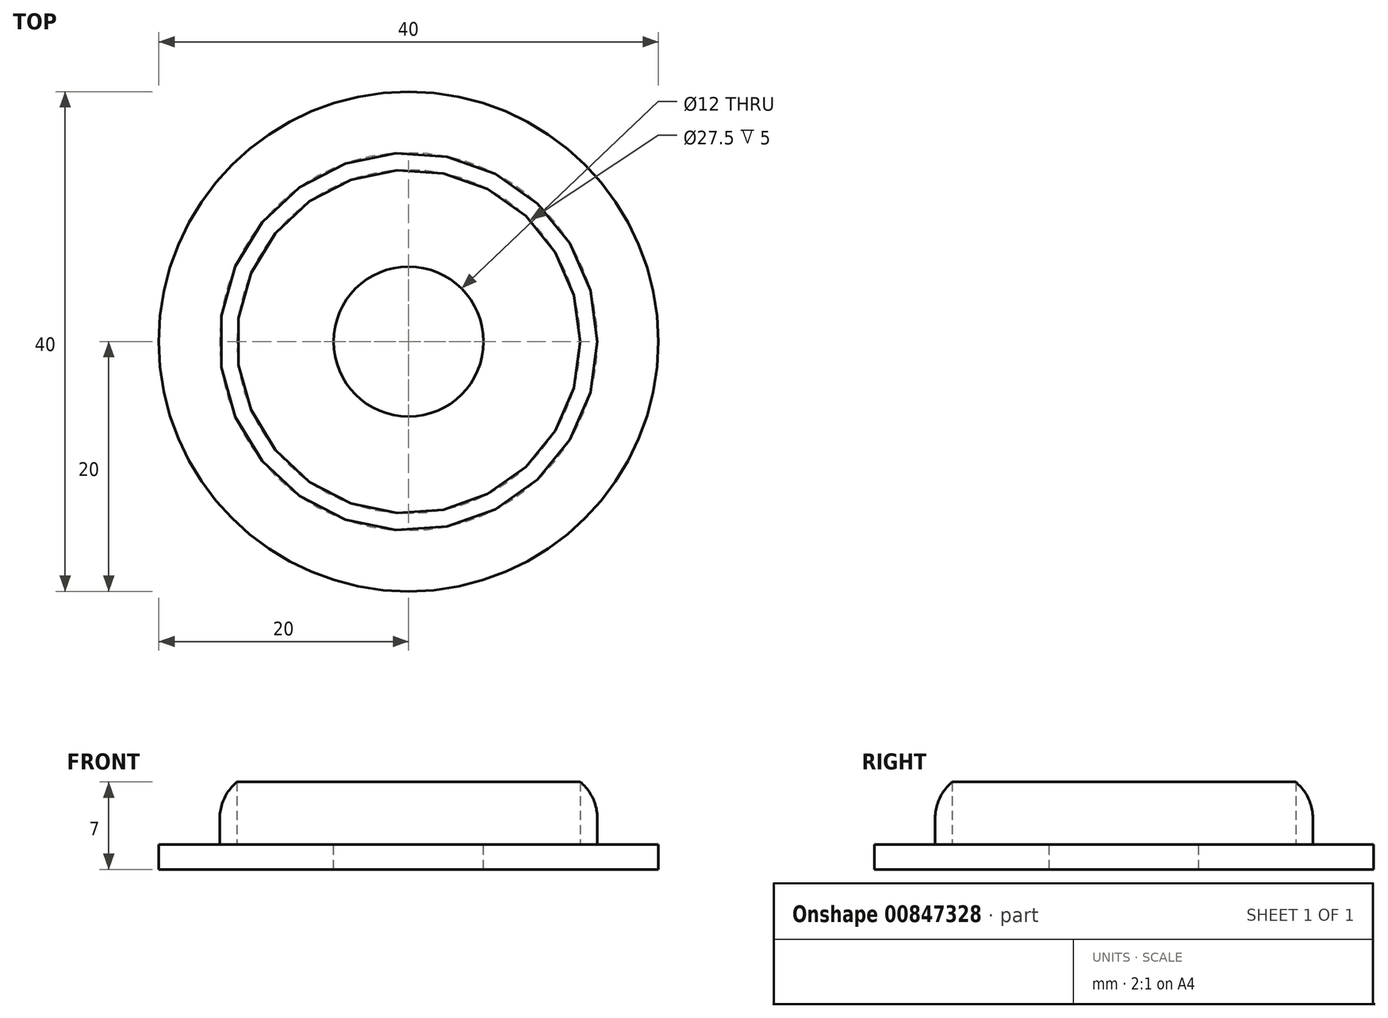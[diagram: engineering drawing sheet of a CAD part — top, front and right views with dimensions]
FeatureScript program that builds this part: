
annotation { "Feature Type Name" : "Feature", "Feature Type Description" : "" }
export const myFeature = defineFeature(function(context is Context, id is Id, definition is map)
    precondition{}
    {
        {
            var Q0;
            Q0=qCreatedBy(makeId("Top.planeOp"),FACE);
            var sketch = newSketch(context, id + "F0", { "sketchPlane" : qUnion([Q0])});
            skCircle(sketch, "E0", {"center": v(0, 0) * mm, "radius": 15.12 * mm});
            skCircle(sketch, "E1", {"center": v(0, 0) * mm, "radius": 20 * mm});
            skCircle(sketch, "E2", {"center": v(0, 0) * mm, "radius": 13.75 * mm});
            skCircle(sketch, "E3", {"center": v(0, 0) * mm, "radius": 6 * mm});
            skSolve(sketch);
        }
        {
            var Q0;
            Q0=makeQuery(id+"F0.imprint","IMPRINT",FACE,{"disambiguationData":[TD([[makeQuery(id+"F0.imprint","IMPRINT",EDGE,{"derivedFrom":sQuery(id+"F0.wireOp",EDGE,"E0")}),1.0]])]});
            extrude(context, id + "F1", {"entities" : qUnion([Q0]), "depth" : 5 * mm, "offsetDistance" : 25 * mm});
        }
        {
            var Q0;
            Q0=makeQuery(id+"F0.imprint","IMPRINT",FACE,{"disambiguationData":[TD([[makeQuery(id+"F0.imprint","IMPRINT",EDGE,{"derivedFrom":sQuery(id+"F0.wireOp",EDGE,"E0")}),1.0]])]});
            var Q1;
            Q1=makeQuery(id+"F0.imprint","IMPRINT",FACE,{"disambiguationData":[TD([[makeQuery(id+"F0.imprint","IMPRINT",EDGE,{"derivedFrom":sQuery(id+"F0.wireOp",EDGE,"E0")}),-1.0]])]});
            var Q2;
            Q2=makeQuery(id+"F0.imprint","IMPRINT",FACE,{"disambiguationData":[TD([[makeQuery(id+"F0.imprint","IMPRINT",EDGE,{"derivedFrom":sQuery(id+"F0.wireOp",EDGE,"E2")}),1.0]])]});
            extrude(context, id + "F2", {"entities" : qUnion([Q0, Q1, Q2]), "oppositeDirection" : true, "depth" : 2 * mm, "offsetDistance" : 25 * mm});
        }
        {
            var Q0;
            Q0=makeQuery(id+"F1.opExtrude","CAP_EDGE",EDGE,{"disambiguationData":[OSD([sQuery(id+"F0.wireOp",EDGE,"E0")])],"isStart":false});
            fillet(context, id + "F3", {"entities" : qUnion([Q0]), "radius" : 4 * mm, "tangentPropagation" : true, "rho" : .5, "crossSection" : FilletCrossSection.CONIC, "allowEdgeOverflow" : false});
        }
    });
